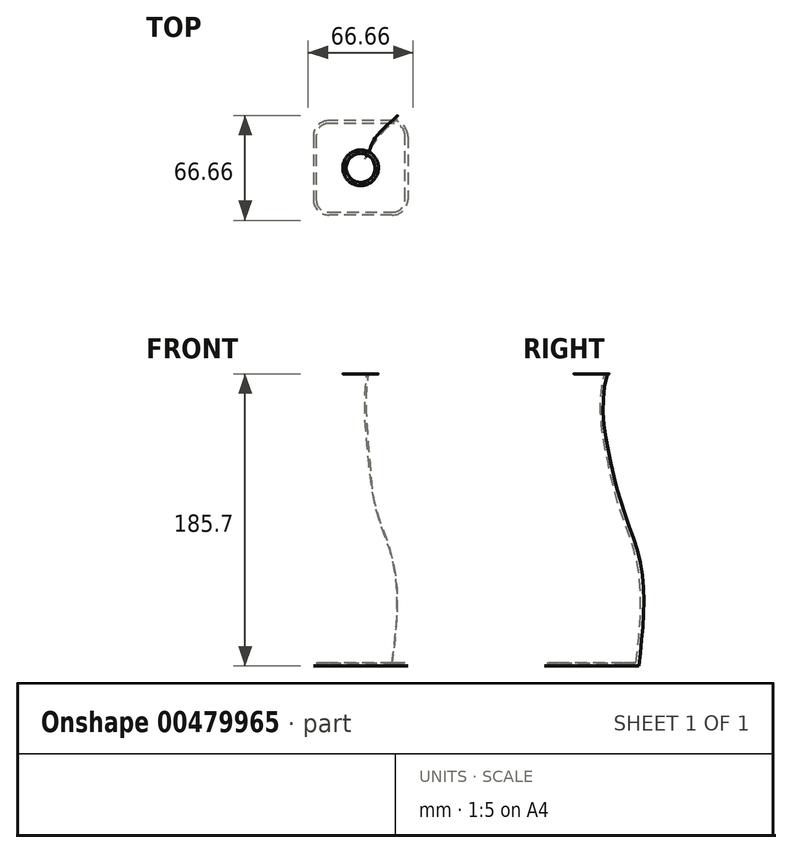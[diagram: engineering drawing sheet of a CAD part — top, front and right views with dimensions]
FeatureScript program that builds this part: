
annotation { "Feature Type Name" : "Feature", "Feature Type Description" : "" }
export const myFeature = defineFeature(function(context is Context, id is Id, definition is map)
    precondition{}
    {
        {
            var Q0;
            Q0=qCreatedBy(makeId("Top.planeOp"),FACE);
            var sketch = newSketch(context, id + "F0", { "sketchPlane" : qUnion([Q0])});
            skLineSegment(sketch, "E0.bottom", {"start": v(20, 30) * mm, "end": v(-20, 30) * mm});
            skLineSegment(sketch, "E0.top", {"start": v(20, -30) * mm, "end": v(-20, -30) * mm});
            skLineSegment(sketch, "E0.left", {"start": v(30, 20) * mm, "end": v(30, -20) * mm});
            skLineSegment(sketch, "E0.right", {"start": v(-30, 20) * mm, "end": v(-30, -20) * mm});
            skPoint(sketch, "E0.middle", {"position": v(0, 0) * mm});
            skPoint(sketch, "E1.visualSharp", {"position": v(30, 30) * mm});
            skArc(sketch, "E1.filletArc", {"start": v(30, 20) * mm, "mid": v(27.07, 27.07) * mm, "end": v(20, 30) * mm});
            skPoint(sketch, "E2.visualSharp", {"position": v(-30, 30) * mm});
            skArc(sketch, "E2.filletArc", {"start": v(-20, 30) * mm, "mid": v(-27.07, 27.07) * mm, "end": v(-30, 20) * mm});
            skPoint(sketch, "E3.visualSharp", {"position": v(-30, -30) * mm});
            skArc(sketch, "E3.filletArc", {"start": v(-30, -20) * mm, "mid": v(-27.07, -27.07) * mm, "end": v(-20, -30) * mm});
            skPoint(sketch, "E4.visualSharp", {"position": v(30, -30) * mm});
            skArc(sketch, "E4.filletArc", {"start": v(20, -30) * mm, "mid": v(27.07, -27.07) * mm, "end": v(30, -20) * mm});
            skSolve(sketch);
        }
        {
            var Q0;
            Q0=qCreatedBy(makeId("Top.planeOp"),FACE);
            cPlane(context, id + "F1", {"entities" : qUnion([Q0]), "cplaneType" : CPlaneType.OFFSET, "offset" : 70 * mm, "width" : 150 * mm, "height" : 150 * mm});
        }
        {
            var Q0;
            Q0=qCreatedBy(id+"F1.planeOp",FACE);
            var sketch = newSketch(context, id + "F2", { "sketchPlane" : qUnion([Q0])});
            skLineSegment(sketch, "E5.bottom", {"start": v(20, 30) * mm, "end": v(-20, 30) * mm});
            skLineSegment(sketch, "E5.top", {"start": v(20, -30) * mm, "end": v(-20, -30) * mm});
            skLineSegment(sketch, "E5.left", {"start": v(30, 20) * mm, "end": v(30, -20) * mm});
            skLineSegment(sketch, "E5.right", {"start": v(-30, 20) * mm, "end": v(-30, -20) * mm});
            skPoint(sketch, "E5.middle", {"position": v(0, 0) * mm});
            skPoint(sketch, "E6.visualSharp", {"position": v(-30, -30) * mm});
            skArc(sketch, "E6.filletArc", {"start": v(-30, -20) * mm, "mid": v(-27.07, -27.07) * mm, "end": v(-20, -30) * mm});
            skPoint(sketch, "E7.visualSharp", {"position": v(-30, 30) * mm});
            skArc(sketch, "E7.filletArc", {"start": v(-20, 30) * mm, "mid": v(-27.07, 27.07) * mm, "end": v(-30, 20) * mm});
            skPoint(sketch, "E8.visualSharp", {"position": v(30, 30) * mm});
            skArc(sketch, "E8.filletArc", {"start": v(30, 20) * mm, "mid": v(27.07, 27.07) * mm, "end": v(20, 30) * mm});
            skPoint(sketch, "E9.visualSharp", {"position": v(30, -30) * mm});
            skArc(sketch, "E9.filletArc", {"start": v(20, -30) * mm, "mid": v(27.07, -27.07) * mm, "end": v(30, -20) * mm});
            skSolve(sketch);
        }
        {
            var Q0;
            Q0=qCreatedBy(id+"F1.planeOp",FACE);
            cPlane(context, id + "F3", {"entities" : qUnion([Q0]), "cplaneType" : CPlaneType.OFFSET, "offset" : 30 * mm, "width" : 150 * mm, "height" : 150 * mm});
        }
        {
            var Q0;
            Q0=qCreatedBy(id+"F3.planeOp",FACE);
            var sketch = newSketch(context, id + "F4", { "sketchPlane" : qUnion([Q0])});
            skLineSegment(sketch, "E10.bottom", {"start": v(10, 20) * mm, "end": v(-10, 20) * mm});
            skLineSegment(sketch, "E10.top", {"start": v(10, -20) * mm, "end": v(-10, -20) * mm});
            skLineSegment(sketch, "E10.left", {"start": v(20, 10) * mm, "end": v(20, -10) * mm});
            skLineSegment(sketch, "E10.right", {"start": v(-20, 10) * mm, "end": v(-20, -10) * mm});
            skPoint(sketch, "E10.middle", {"position": v(0, 0) * mm});
            skPoint(sketch, "E11.visualSharp", {"position": v(-20, 20) * mm});
            skArc(sketch, "E11.filletArc", {"start": v(-10, 20) * mm, "mid": v(-17.07, 17.07) * mm, "end": v(-20, 10) * mm});
            skPoint(sketch, "E12.visualSharp", {"position": v(20, 20) * mm});
            skArc(sketch, "E12.filletArc", {"start": v(20, 10) * mm, "mid": v(17.07, 17.07) * mm, "end": v(10, 20) * mm});
            skPoint(sketch, "E13.visualSharp", {"position": v(20, -20) * mm});
            skArc(sketch, "E13.filletArc", {"start": v(10, -20) * mm, "mid": v(17.07, -17.07) * mm, "end": v(20, -10) * mm});
            skPoint(sketch, "E14.visualSharp", {"position": v(-20, -20) * mm});
            skArc(sketch, "E14.filletArc", {"start": v(-20, -10) * mm, "mid": v(-17.07, -17.07) * mm, "end": v(-10, -20) * mm});
            skSolve(sketch);
        }
        {
            var Q0;
            Q0=makeQuery(id+"F4.imprint","IMPRINT",FACE,{"disambiguationData":[TD([[makeQuery(id+"F4.imprint","IMPRINT",EDGE,{"derivedFrom":sQuery(id+"F4.wireOp",EDGE,"E10.bottom")}),1.0]])]});
            cPlane(context, id + "F5", {"entities" : qUnion([Q0]), "cplaneType" : CPlaneType.OFFSET, "offset" : 30 * mm, "width" : 150 * mm, "height" : 150 * mm});
        }
        {
            var Q0;
            Q0=qCreatedBy(id+"F5.planeOp",FACE);
            var sketch = newSketch(context, id + "F6", { "sketchPlane" : qUnion([Q0])});
            skCircle(sketch, "E15", {"center": v(0, 0) * mm, "radius": 13.45 * mm});
            skSolve(sketch);
        }
        {
            var Q0;
            Q0=qCreatedBy(id+"F5.planeOp",FACE);
            cPlane(context, id + "F7", {"entities" : qUnion([Q0]), "cplaneType" : CPlaneType.OFFSET, "offset" : 52 * mm, "width" : 150 * mm, "height" : 150 * mm});
        }
        {
            var Q0;
            Q0=qCreatedBy(id+"F7.planeOp",FACE);
            var sketch = newSketch(context, id + "F8", { "sketchPlane" : qUnion([Q0])});
            skCircle(sketch, "E16", {"center": v(0, 0) * mm, "radius": 10.25 * mm});
            skSolve(sketch);
        }
        {
            var Q0;
            Q0=qCreatedBy(id+"F3.planeOp",FACE);
            cPlane(context, id + "F9", {"entities" : qUnion([Q0]), "cplaneType" : CPlaneType.OFFSET, "offset" : 85.7 * mm, "width" : 150 * mm, "height" : 150 * mm});
        }
        {
            var Q0;
            Q0=qCreatedBy(id+"F9.planeOp",FACE);
            var sketch = newSketch(context, id + "F10", { "sketchPlane" : qUnion([Q0])});
            skCircle(sketch, "E17", {"center": v(0, 0) * mm, "radius": 11.31 * mm});
            skSolve(sketch);
        }
        {
            var Q0;
            Q0=makeQuery(id+"F0.imprint","IMPRINT",FACE,{"disambiguationData":[TD([[makeQuery(id+"F0.imprint","IMPRINT",EDGE,{"derivedFrom":sQuery(id+"F0.wireOp",EDGE,"E0.bottom")}),1.0]])]});
            var Q1;
            Q1=makeQuery(id+"F2.imprint","IMPRINT",FACE,{"disambiguationData":[TD([[makeQuery(id+"F2.imprint","IMPRINT",EDGE,{"derivedFrom":sQuery(id+"F2.wireOp",EDGE,"E5.bottom")}),1.0]])]});
            var Q2;
            Q2=makeQuery(id+"F4.imprint","IMPRINT",FACE,{"disambiguationData":[TD([[makeQuery(id+"F4.imprint","IMPRINT",EDGE,{"derivedFrom":sQuery(id+"F4.wireOp",EDGE,"E10.bottom")}),1.0]])]});
            var Q3;
            Q3=makeQuery(id+"F6.imprint","IMPRINT",FACE,{"disambiguationData":[TD([[makeQuery(id+"F6.imprint","IMPRINT",EDGE,{"derivedFrom":sQuery(id+"F6.wireOp",EDGE,"E15")}),1.0]])]});
            var Q4;
            Q4=makeQuery(id+"F8.imprint","IMPRINT",FACE,{"disambiguationData":[TD([[makeQuery(id+"F8.imprint","IMPRINT",EDGE,{"derivedFrom":sQuery(id+"F8.wireOp",EDGE,"E16")}),1.0]])]});
            var Q5;
            Q5=makeQuery(id+"F10.imprint","IMPRINT",FACE,{"disambiguationData":[TD([[makeQuery(id+"F10.imprint","IMPRINT",EDGE,{"derivedFrom":sQuery(id+"F10.wireOp",EDGE,"E17")}),1.0]])]});
            loft(context, id + "F11", {"sheetProfilesArray" : [{ "sheetProfileEntities" : qUnion([Q0]) }, { "sheetProfileEntities" : qUnion([Q1]) }, { "sheetProfileEntities" : qUnion([Q2]) }, { "sheetProfileEntities" : qUnion([Q3]) }, { "sheetProfileEntities" : qUnion([Q4]) }, { "sheetProfileEntities" : qUnion([Q5]) }]});
        }
        {
            var Q0;
            Q0=makeQuery(id+"F11.opLoft","CAP_FACE",FACE,{"disambiguationData":[OSD([makeQuery(id+"F10.imprint","IMPRINT",FACE,{"disambiguationData":[TD([[makeQuery(id+"F10.imprint","IMPRINT",EDGE,{"derivedFrom":sQuery(id+"F10.wireOp",EDGE,"E17")}),1.0]])]})])],"isStart":true});
            shell(context, id + "F12", {"entities" : qUnion([Q0]), "thickness" : 2 * mm});
        }
    });
